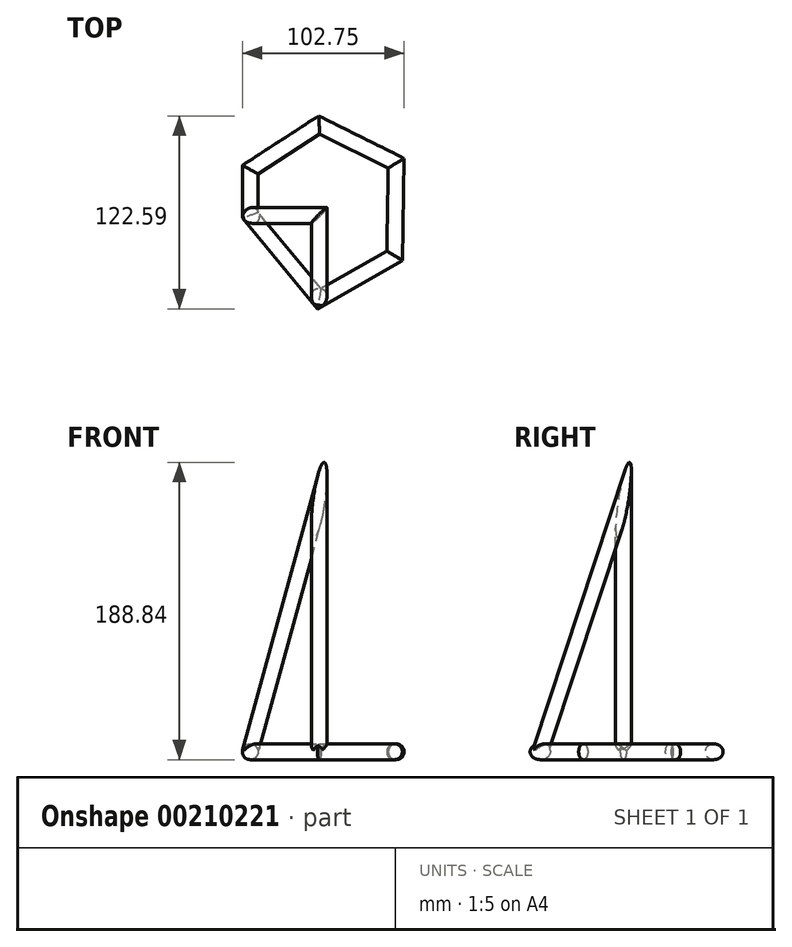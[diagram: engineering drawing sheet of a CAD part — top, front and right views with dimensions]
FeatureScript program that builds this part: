
annotation { "Feature Type Name" : "Feature", "Feature Type Description" : "" }
export const myFeature = defineFeature(function(context is Context, id is Id, definition is map)
    precondition{}
    {
        {
            var Q0;
            Q0=qCreatedBy(makeId("Front.planeOp"),FACE);
            var sketch = newSketch(context, id + "F0", { "sketchPlane" : qUnion([Q0])});
            skLineSegment(sketch, "E0", {"start": v(0, 0) * mm, "end": v(0, 160) * mm});
            skSolve(sketch);
        }
        {
            var Q0;
            Q0=qCreatedBy(makeId("Top.planeOp"),FACE);
            var sketch = newSketch(context, id + "F1", { "sketchPlane" : qUnion([Q0])});
            skLineSegment(sketch, "E1", {"start": v(-43.8, 29.15) * mm, "end": v(0, 57.51) * mm});
            skLineSegment(sketch, "E2", {"start": v(0, 57.51) * mm, "end": v(48.89, 33.2) * mm});
            skLineSegment(sketch, "E3", {"start": v(48.89, 33.2) * mm, "end": v(47.87, -25.55) * mm});
            skLineSegment(sketch, "E4", {"start": v(47.87, -25.55) * mm, "end": v(0, -52.9) * mm});
            skLineSegment(sketch, "E5", {"start": v(0, -52.9) * mm, "end": v(-43.8, 0) * mm});
            skLineSegment(sketch, "E6", {"start": v(-43.8, 0) * mm, "end": v(-43.8, 29.15) * mm});
            skSolve(sketch);
        }
        {
            var Q0;
            Q0=sQuery(id+"F1.wireOp",VERTEX,"E1.start");
            var Q1;
            Q1=sQuery(id+"F0.wireOp",VERTEX,"E0.end");
            var Q2;
            Q2=sQuery(id+"F0.wireOp",VERTEX,"E0.start");
            cPlane(context, id + "F2", {"entities" : qUnion([Q0, Q1, Q2]), "cplaneType" : CPlaneType.THREE_POINT, "offset" : 25 * mm, "width" : 150 * mm, "height" : 150 * mm});
        }
        {
            var Q0;
            Q0=sQuery(id+"F1.wireOp",VERTEX,"E3.start");
            var Q1;
            Q1=sQuery(id+"F0.wireOp",VERTEX,"E0.end");
            var Q2;
            Q2=sQuery(id+"F0.wireOp",VERTEX,"E0.start");
            cPlane(context, id + "F3", {"entities" : qUnion([Q0, Q1, Q2]), "cplaneType" : CPlaneType.THREE_POINT, "offset" : 25 * mm, "width" : 150 * mm, "height" : 150 * mm});
        }
        {
            var Q0;
            Q0=sQuery(id+"F1.wireOp",VERTEX,"E4.start");
            var Q1;
            Q1=sQuery(id+"F0.wireOp",VERTEX,"E0.start");
            var Q2;
            Q2=sQuery(id+"F0.wireOp",VERTEX,"E0.end");
            cPlane(context, id + "F4", {"entities" : qUnion([Q0, Q1, Q2]), "cplaneType" : CPlaneType.THREE_POINT, "offset" : 25 * mm, "width" : 150 * mm, "height" : 150 * mm});
        }
        {
            var Q0;
            Q0=qCreatedBy(id+"F3.planeOp",FACE);
            var sketch = newSketch(context, id + "F5", { "sketchPlane" : qUnion([Q0])});
            skLineSegment(sketch, "E7", {"start": v(-59.1, 0) * mm, "end": v(0, 160) * mm});
            skSolve(sketch);
        }
        {
            var Q0;
            Q0=qCreatedBy(makeId("Right.planeOp"),FACE);
            var sketch = newSketch(context, id + "F6", { "sketchPlane" : qUnion([Q0])});
            skLineSegment(sketch, "E8", {"start": v(57.51, 0) * mm, "end": v(0, 160) * mm});
            skSolve(sketch);
        }
        {
            var Q0;
            Q0=qCreatedBy(id+"F4.planeOp",FACE);
            var sketch = newSketch(context, id + "F7", { "sketchPlane" : qUnion([Q0])});
            skLineSegment(sketch, "E9", {"start": v(0, 160) * mm, "end": v(54.27, 0) * mm});
            skSolve(sketch);
        }
        {
            var Q0;
            Q0=qCreatedBy(id+"F2.planeOp",FACE);
            var sketch = newSketch(context, id + "F8", { "sketchPlane" : qUnion([Q0])});
            skLineSegment(sketch, "E10", {"start": v(0, 160) * mm, "end": v(-52.62, 0) * mm});
            skSolve(sketch);
        }
        {
            var Q0;
            Q0=qCreatedBy(makeId("Right.planeOp"),FACE);
            var sketch = newSketch(context, id + "F9", { "sketchPlane" : qUnion([Q0])});
            skLineSegment(sketch, "E11", {"start": v(-52.9, 0) * mm, "end": v(0, 160) * mm});
            skSolve(sketch);
        }
        {
            var Q0;
            Q0=qCreatedBy(makeId("Front.planeOp"),FACE);
            var sketch = newSketch(context, id + "F10", { "sketchPlane" : qUnion([Q0])});
            skLineSegment(sketch, "E12", {"start": v(-43.8, 0) * mm, "end": v(0, 160) * mm});
            skSolve(sketch);
        }
        {
            var Q0;
            Q0=sQuery(id+"F1.wireOp",EDGE,"E5");
            var Q1;
            Q1=sQuery(id+"F9.wireOp",VERTEX,"E11.start");
            cPlane(context, id + "F11", {"entities" : qUnion([Q0, Q1]), "cplaneType" : CPlaneType.LINE_POINT, "offset" : 25 * mm, "width" : 150 * mm, "height" : 150 * mm});
        }
        {
            var Q0;
            Q0=qCreatedBy(id+"F11.planeOp",FACE);
            var sketch = newSketch(context, id + "F12", { "sketchPlane" : qUnion([Q0])});
            skCircle(sketch, "E13", {"center": v(33.74, 0) * mm, "radius": 5 * mm});
            skSolve(sketch);
        }
        {
            var Q0;
            Q0=makeQuery(id+"F12.imprint","IMPRINT",FACE,{"disambiguationData":[TD([[makeQuery(id+"F12.imprint","IMPRINT",EDGE,{"derivedFrom":sQuery(id+"F12.wireOp",EDGE,"E13")}),1.0]])]});
            var Q1;
            Q1=sQuery(id+"F1.wireOp",EDGE,"E5");
            var Q2;
            Q2=sQuery(id+"F1.wireOp",EDGE,"E6");
            var Q3;
            Q3=sQuery(id+"F1.wireOp",EDGE,"E1");
            var Q4;
            Q4=sQuery(id+"F1.wireOp",EDGE,"E2");
            var Q5;
            Q5=sQuery(id+"F1.wireOp",EDGE,"E3");
            var Q6;
            Q6=sQuery(id+"F1.wireOp",EDGE,"E4");
            sweep(context, id + "F13", {"profiles" : qUnion([Q0]), "path" : qUnion([Q1, Q2, Q3, Q4, Q5, Q6])});
        }
        {
            var Q0;
            Q0=sQuery(id+"F10.wireOp",EDGE,"E12");
            var Q1;
            Q1=sQuery(id+"F10.wireOp",VERTEX,"E12.start");
            cPlane(context, id + "F14", {"entities" : qUnion([Q0, Q1]), "cplaneType" : CPlaneType.LINE_POINT, "offset" : 25 * mm, "width" : 150 * mm, "height" : 150 * mm});
        }
        {
            var Q0;
            Q0=qCreatedBy(id+"F14.planeOp",FACE);
            var sketch = newSketch(context, id + "F15", { "sketchPlane" : qUnion([Q0])});
            skCircle(sketch, "E14", {"center": v(-42.25, 0) * mm, "radius": 5 * mm});
            skSolve(sketch);
        }
        {
            var Q0;
            Q0=makeQuery(id+"F15.imprint","IMPRINT",FACE,{"disambiguationData":[TD([[makeQuery(id+"F15.imprint","IMPRINT",EDGE,{"derivedFrom":sQuery(id+"F15.wireOp",EDGE,"E14")}),1.0]])]});
            var Q1;
            Q1=sQuery(id+"F10.wireOp",EDGE,"E12");
            var Q2;
            Q2=sQuery(id+"F9.wireOp",EDGE,"E11");
            sweep(context, id + "F16", {"operationType" : NewBodyOperationType.ADD, "profiles" : qUnion([Q0]), "path" : qUnion([Q1, Q2])});
        }
    });
